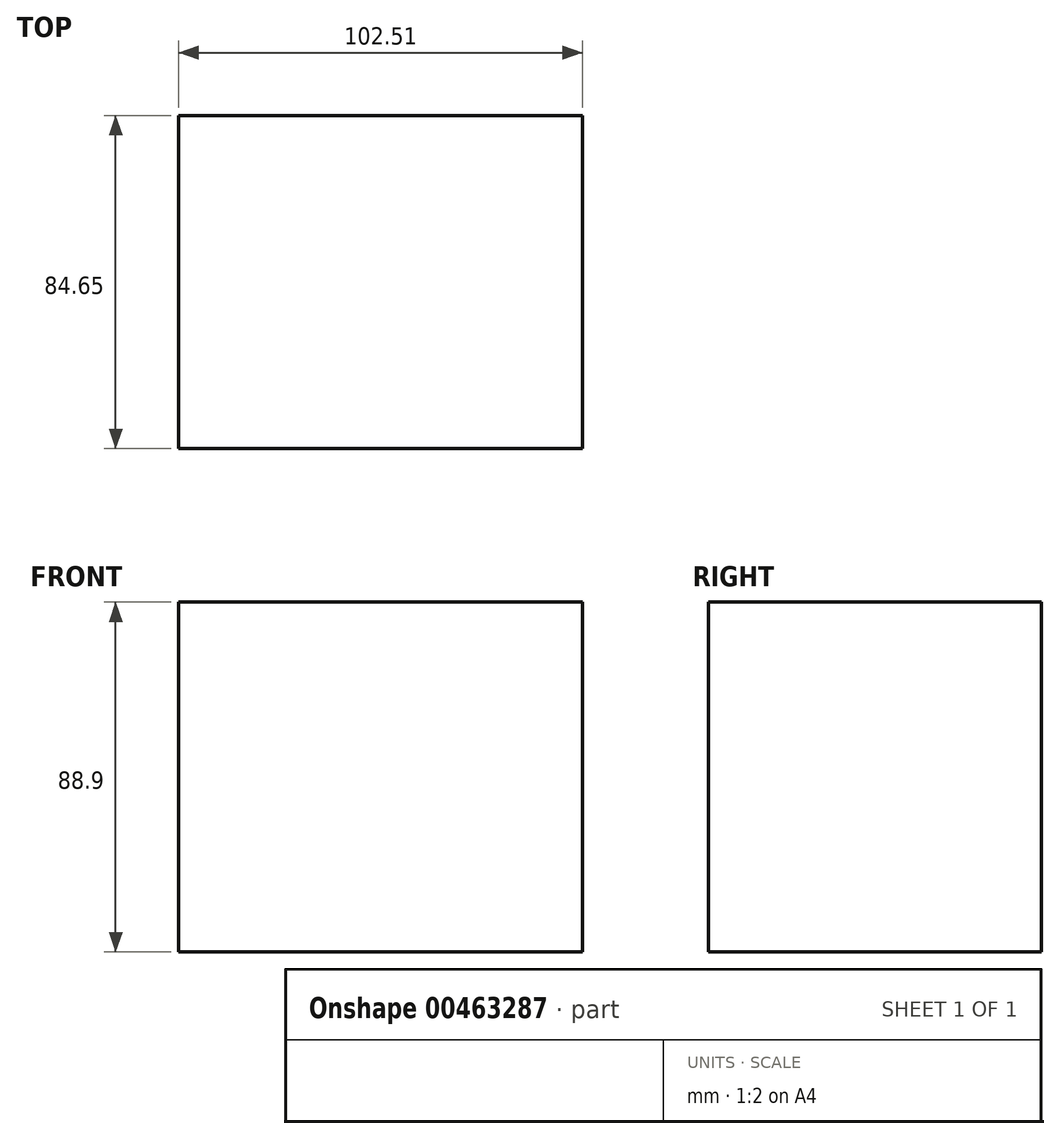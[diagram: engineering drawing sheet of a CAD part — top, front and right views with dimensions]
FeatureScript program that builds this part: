
annotation { "Feature Type Name" : "Feature", "Feature Type Description" : "" }
export const myFeature = defineFeature(function(context is Context, id is Id, definition is map)
    precondition{}
    {
        {
            var Q0;
            Q0=qCreatedBy(makeId("Top.planeOp"),FACE);
            var sketch = newSketch(context, id + "F0", { "sketchPlane" : qUnion([Q0])});
            skLineSegment(sketch, "E0", {"start": v(0, 0) * mm, "end": v(0, -84.65) * mm});
            skLineSegment(sketch, "E1", {"start": v(0, -84.65) * mm, "end": v(102.5, -84.65) * mm});
            skLineSegment(sketch, "E2", {"start": v(102.5, 0) * mm, "end": v(0, 0) * mm});
            skLineSegment(sketch, "E3", {"start": v(102.5, 0) * mm, "end": v(102.5, -84.65) * mm});
            skSolve(sketch);
        }
        {
            var Q0;
            Q0=makeQuery(id+"F0.imprint","IMPRINT",FACE,{"disambiguationData":[TD([[makeQuery(id+"F0.imprint","IMPRINT",EDGE,{"derivedFrom":sQuery(id+"F0.wireOp",EDGE,"E0")}),1.0]])]});
            extrude(context, id + "F1", {"entities" : qUnion([Q0]), "depth" : 50.8 * mm, "hasSecondDirection" : true, "secondDirectionOppositeDirection" : true, "secondDirectionDepth" : 38.1 * mm});
        }
        {
            var Q0;
            Q0=makeQuery(id+"F1.opExtrude","SWEPT_FACE",FACE,{"disambiguationData":[OSD([sQuery(id+"F0.wireOp",EDGE,"E1")])]});
            var sketch = newSketch(context, id + "F2", { "sketchPlane" : qUnion([Q0])});
            skCircle(sketch, "E4", {"center": v(56, 6.27) * mm, "radius": 27.08 * mm});
            skSolve(sketch);
        }
        {
            var Q0;
            Q0=sQuery(id+"F2.wireOp",EDGE,"E4");
            extrude(context, id + "F3", {"bodyType" : ToolBodyType.SURFACE, "surfaceEntities" : qUnion([Q0]), "endBound" : BoundingType.THROUGH_ALL, "oppositeDirection" : true, "depth" : 25.4 * mm});
        }
    });
